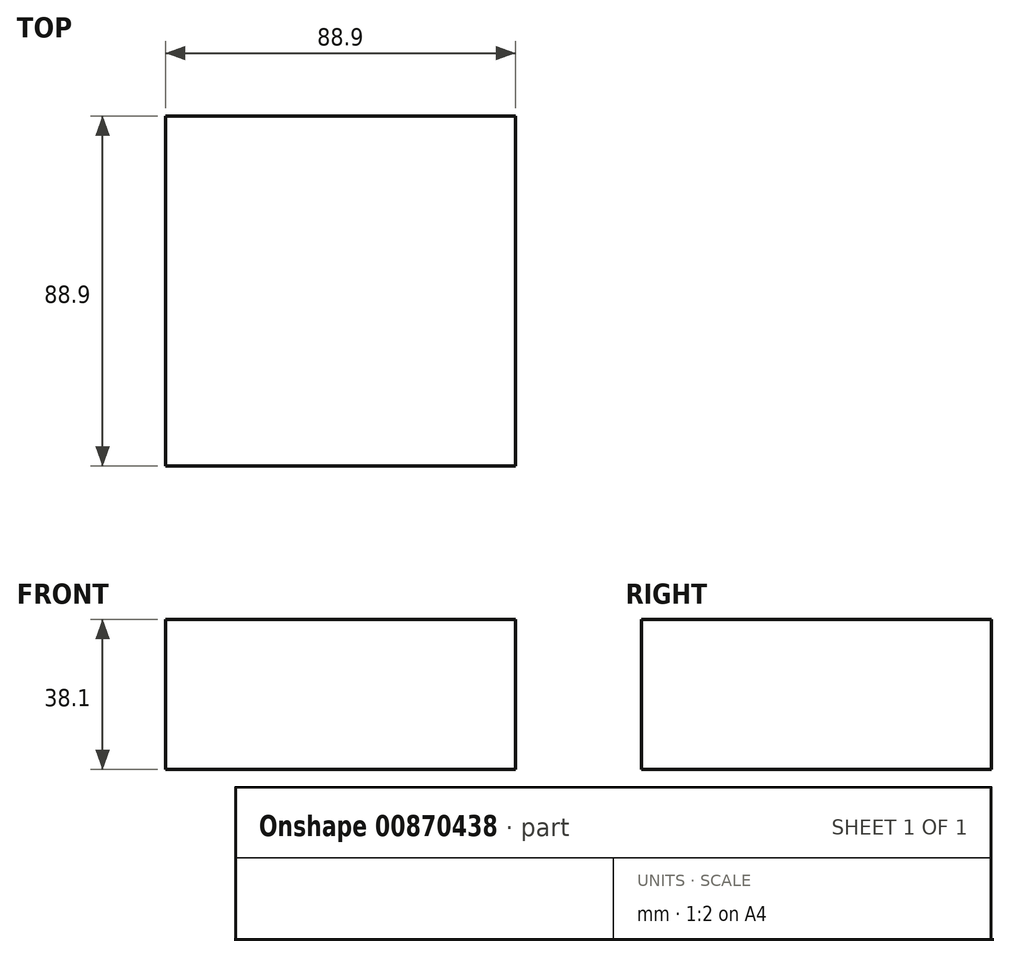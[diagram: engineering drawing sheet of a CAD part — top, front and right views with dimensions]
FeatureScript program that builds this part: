
annotation { "Feature Type Name" : "Feature", "Feature Type Description" : "" }
export const myFeature = defineFeature(function(context is Context, id is Id, definition is map)
    precondition{}
    {
        {
            var Q0;
            Q0=qCreatedBy(makeId("Right.planeOp"),FACE);
            var sketch = newSketch(context, id + "F0", { "sketchPlane" : qUnion([Q0])});
            skLineSegment(sketch, "E0.bottom", {"start": v(46.26, 19.05) * mm, "end": v(-42.64, 19.05) * mm});
            skLineSegment(sketch, "E0.top", {"start": v(46.26, -19.05) * mm, "end": v(-42.64, -19.05) * mm});
            skLineSegment(sketch, "E0.left", {"start": v(46.26, 19.05) * mm, "end": v(46.26, -19.05) * mm});
            skLineSegment(sketch, "E0.right", {"start": v(-42.64, 19.05) * mm, "end": v(-42.64, -19.05) * mm});
            skPoint(sketch, "E0.middle", {"position": v(1.8, 0) * mm});
            skSolve(sketch);
        }
        {
            var Q0;
            Q0=makeQuery(id+"F0.imprint","IMPRINT",FACE,{"disambiguationData":[TD([[makeQuery(id+"F0.imprint","IMPRINT",EDGE,{"derivedFrom":sQuery(id+"F0.wireOp",EDGE,"E0.bottom")}),1.0]])]});
            extrude(context, id + "F1", {"entities" : qUnion([Q0]), "depth" : 88.9 * mm, "offsetDistance" : 25.4 * mm});
        }
    });
